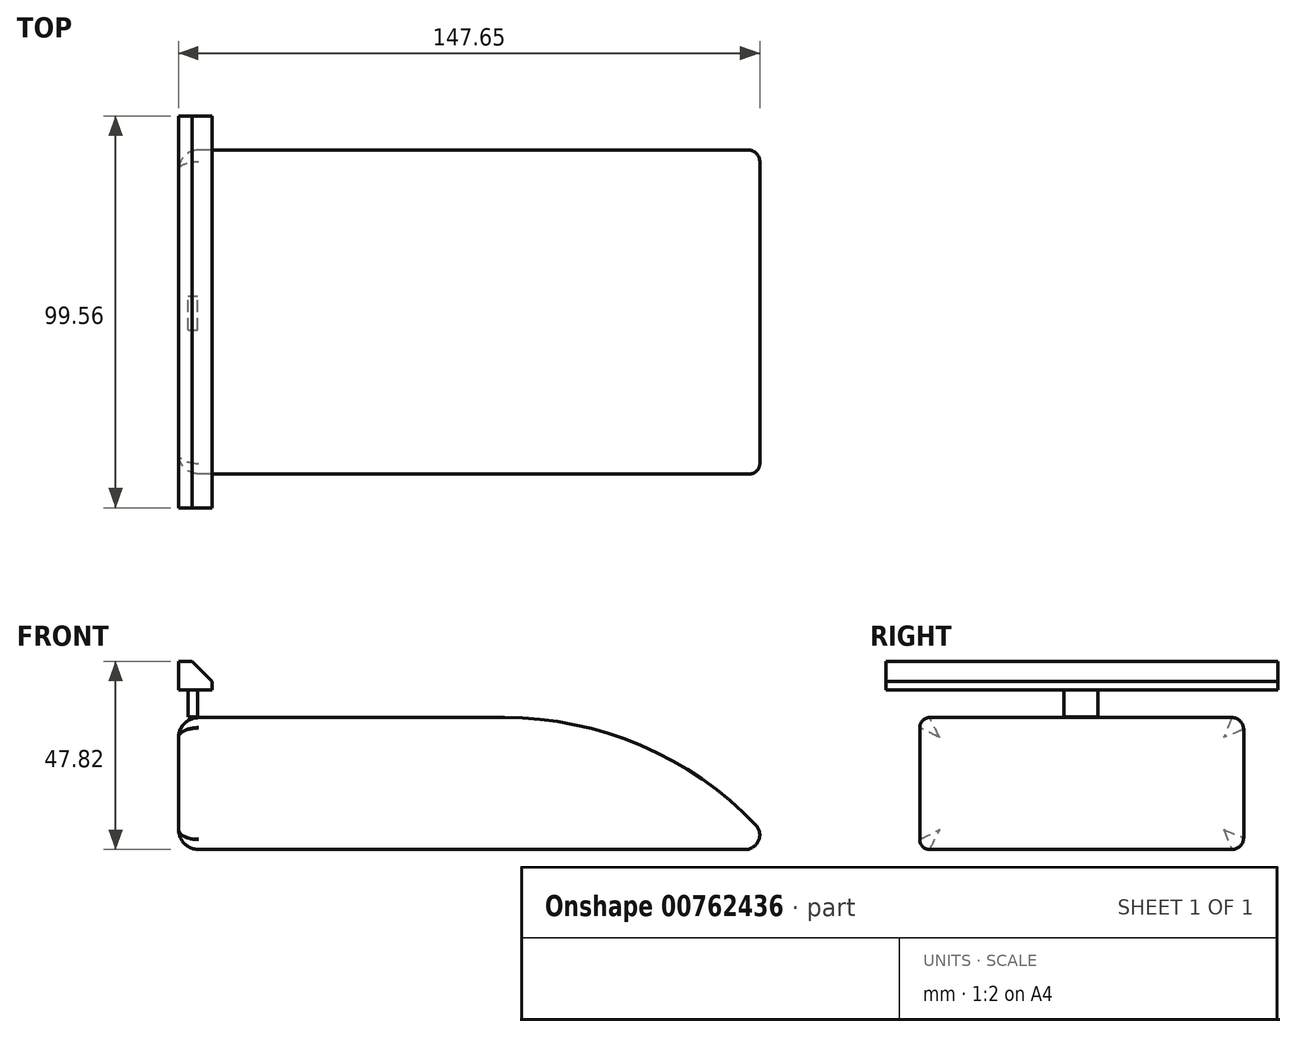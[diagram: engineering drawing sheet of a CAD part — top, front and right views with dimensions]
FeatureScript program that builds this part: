
annotation { "Feature Type Name" : "Feature", "Feature Type Description" : "" }
export const myFeature = defineFeature(function(context is Context, id is Id, definition is map)
    precondition{}
    {
        {
            var Q0;
            Q0=qCreatedBy(makeId("Front.planeOp"),FACE);
            var sketch = newSketch(context, id + "F0", { "sketchPlane" : qUnion([Q0])});
            skLineSegment(sketch, "E0.bottom", {"start": v(76.1, 0) * mm, "end": v(-76, 0) * mm});
            skLineSegment(sketch, "E0.top", {"start": v(76.1, 33.52) * mm, "end": v(-76, 33.52) * mm});
            skLineSegment(sketch, "E0.left", {"start": v(76.1, 0) * mm, "end": v(76.1, 33.52) * mm});
            skLineSegment(sketch, "E0.right", {"start": v(-76, 0) * mm, "end": v(-76, 33.52) * mm});
            skSolve(sketch);
        }
        {
            var Q0;
            Q0=makeQuery(id+"F0.imprint","IMPRINT",FACE,{"disambiguationData":[TD([[makeQuery(id+"F0.imprint","IMPRINT",EDGE,{"derivedFrom":sQuery(id+"F0.wireOp",EDGE,"E0.bottom")}),-1.0]])]});
            extrude(context, id + "F1", {"entities" : qUnion([Q0]), "depth" : 41.15 * mm, "offsetDistance" : 25.4 * mm});
        }
        {
            var Q0;
            Q0=makeQuery(id+"F1.opExtrude","CAP_FACE",FACE,{"disambiguationData":[OSD([sQuery(id+"F0.wireOp",EDGE,"E0.bottom"),sQuery(id+"F0.wireOp",EDGE,"E0.top"),sQuery(id+"F0.wireOp",EDGE,"E0.left"),sQuery(id+"F0.wireOp",EDGE,"E0.right")])],"isStart":true});
            extrude(context, id + "F2", {"entities" : qUnion([Q0]), "operationType" : NewBodyOperationType.ADD, "depth" : 41.15 * mm, "offsetDistance" : 25.4 * mm});
        }
        {
            var Q0;
            {var subQ0=sQuery(id+"F0.wireOp",EDGE,"E0.left");var subQ1=sQuery(id+"F0.wireOp",EDGE,"E0.top");Q0=makeQuery(id+"F2.boolean.opBoolean","MERGE",EDGE,{"derivedFrom":[makeQuery(id+"F1.opExtrude","SWEPT_EDGE",EDGE,{"disambiguationData":[OSD([subQ1,subQ0])]}),makeQuery(id+"F2.opExtrude","SWEPT_EDGE",EDGE,{"disambiguationData":[OSD([subQ1,subQ0])]})]});}
            fillet(context, id + "F3", {"entities" : qUnion([Q0]), "radius" : 88.3 * mm, "tangentPropagation" : true, "allowEdgeOverflow" : false});
        }
        {
            var Q0;
            Q0=qCreatedBy(makeId("Front.planeOp"),FACE);
            var sketch = newSketch(context, id + "F4", { "sketchPlane" : qUnion([Q0])});
            skLineSegment(sketch, "E1.bottom", {"start": v(-76, 47.82) * mm, "end": v(-67.5, 47.82) * mm});
            skLineSegment(sketch, "E1.top", {"start": v(-76, 40.52) * mm, "end": v(-67.5, 40.52) * mm});
            skLineSegment(sketch, "E1.left", {"start": v(-76, 47.82) * mm, "end": v(-76, 40.52) * mm});
            skLineSegment(sketch, "E1.right", {"start": v(-67.5, 47.82) * mm, "end": v(-67.5, 40.52) * mm});
            skSolve(sketch);
        }
        {
            var Q0;
            Q0=makeQuery(id+"F4.imprint","IMPRINT",FACE,{"disambiguationData":[TD([[makeQuery(id+"F4.imprint","IMPRINT",EDGE,{"derivedFrom":sQuery(id+"F4.wireOp",EDGE,"E1.bottom")}),-1.0]])]});
            extrude(context, id + "F5", {"entities" : qUnion([Q0]), "depth" : 49.78 * mm, "offsetDistance" : 25.4 * mm});
        }
        {
            var Q0;
            Q0=makeQuery(id+"F5.opExtrude","CAP_FACE",FACE,{"disambiguationData":[OSD([sQuery(id+"F4.wireOp",EDGE,"E1.bottom"),sQuery(id+"F4.wireOp",EDGE,"E1.top"),sQuery(id+"F4.wireOp",EDGE,"E1.left"),sQuery(id+"F4.wireOp",EDGE,"E1.right")])],"isStart":true});
            extrude(context, id + "F6", {"entities" : qUnion([Q0]), "operationType" : NewBodyOperationType.ADD, "depth" : 49.78 * mm, "offsetDistance" : 25.4 * mm});
        }
        {
            var Q0;
            Q0=qCreatedBy(makeId("Front.planeOp"),FACE);
            var sketch = newSketch(context, id + "F7", { "sketchPlane" : qUnion([Q0])});
            skLineSegment(sketch, "E2.bottom", {"start": v(-73.56, 40.56) * mm, "end": v(-71.16, 40.56) * mm});
            skLineSegment(sketch, "E2.top", {"start": v(-73.56, 33.66) * mm, "end": v(-71.16, 33.66) * mm});
            skLineSegment(sketch, "E2.left", {"start": v(-73.56, 40.56) * mm, "end": v(-73.56, 33.66) * mm});
            skLineSegment(sketch, "E2.right", {"start": v(-71.16, 40.56) * mm, "end": v(-71.16, 33.66) * mm});
            skSolve(sketch);
        }
        {
            var Q0;
            Q0 = qSketchRegion(id + "F7", true);
            extrude(context, id + "F8", {"entities" : qUnion([Q0]), "operationType" : NewBodyOperationType.ADD, "depth" : 4.57 * mm, "offsetDistance" : 25.4 * mm});
        }
        {
            var Q0;
            Q0 = qSketchRegion(id + "F7", true);
            extrude(context, id + "F9", {"entities" : qUnion([Q0]), "operationType" : NewBodyOperationType.ADD, "oppositeDirection" : true, "depth" : 4.06 * mm, "offsetDistance" : 25.4 * mm});
        }
        {
            var Q0;
            {var subQ0=sQuery(id+"F4.wireOp",EDGE,"E1.right");var subQ1=sQuery(id+"F4.wireOp",EDGE,"E1.bottom");Q0=makeQuery(id+"F6.boolean.opBoolean","MERGE",EDGE,{"derivedFrom":[makeQuery(id+"F5.opExtrude","SWEPT_EDGE",EDGE,{"disambiguationData":[OSD([subQ1,subQ0])]}),makeQuery(id+"F6.opExtrude","SWEPT_EDGE",EDGE,{"disambiguationData":[OSD([subQ1,subQ0])]})]});}
            chamfer(context, id + "F10", {"entities" : qUnion([Q0]), "width" : 5.08 * mm, "tangentPropagation" : true});
        }
        {
            var Q0;
            {var subQ0=sQuery(id+"F0.wireOp",EDGE,"E0.bottom");var subQ1=sQuery(id+"F0.wireOp",EDGE,"E0.left");var subQ2=sQuery(id+"F0.wireOp",EDGE,"E0.top");Q0=makeQuery(id+"F3.opFillet","BLEND_EDGE",EDGE,{"blendedFrom":[makeQuery(id+"F2.boolean.opBoolean","MERGE",EDGE,{"derivedFrom":[makeQuery(id+"F1.opExtrude","SWEPT_EDGE",EDGE,{"disambiguationData":[OSD([subQ2,subQ1])]}),makeQuery(id+"F2.opExtrude","SWEPT_EDGE",EDGE,{"disambiguationData":[OSD([subQ2,subQ1])]})]}),makeQuery(id+"F2.boolean.opBoolean","MERGE",FACE,{"derivedFrom":[makeQuery(id+"F1.opExtrude","SWEPT_FACE",FACE,{"disambiguationData":[OSD([subQ0])]}),makeQuery(id+"F2.opExtrude","SWEPT_FACE",FACE,{"disambiguationData":[OSD([subQ0])]})]})],"blendedInto":[makeQuery(id+"F2.boolean.opBoolean","MERGE",FACE,{"derivedFrom":[makeQuery(id+"F1.opExtrude","SWEPT_FACE",FACE,{"disambiguationData":[OSD([subQ0])]}),makeQuery(id+"F2.opExtrude","SWEPT_FACE",FACE,{"disambiguationData":[OSD([subQ0])]})]})]});}
            fillet(context, id + "F11", {"entities" : qUnion([Q0]), "radius" : 3.73 * mm, "tangentPropagation" : true, "allowEdgeOverflow" : false});
        }
        {
            var Q0;
            Q0=makeQuery(id+"F1.opExtrude","CAP_EDGE",EDGE,{"disambiguationData":[OSD([sQuery(id+"F0.wireOp",EDGE,"E0.top")])],"isStart":false});
            var Q1;
            {var subQ0=sQuery(id+"F0.wireOp",EDGE,"E0.left");var subQ1=sQuery(id+"F0.wireOp",EDGE,"E0.top");Q1=makeQuery(id+"F3.opFillet","BLEND_EDGE",EDGE,{"blendedFrom":[makeQuery(id+"F2.boolean.opBoolean","MERGE",EDGE,{"derivedFrom":[makeQuery(id+"F1.opExtrude","SWEPT_EDGE",EDGE,{"disambiguationData":[OSD([subQ1,subQ0])]}),makeQuery(id+"F2.opExtrude","SWEPT_EDGE",EDGE,{"disambiguationData":[OSD([subQ1,subQ0])]})]}),makeQuery(id+"F1.opExtrude","CAP_FACE",FACE,{"disambiguationData":[OSD([sQuery(id+"F0.wireOp",EDGE,"E0.bottom"),subQ1,subQ0,sQuery(id+"F0.wireOp",EDGE,"E0.right")])],"isStart":false})],"blendedInto":[makeQuery(id+"F1.opExtrude","CAP_FACE",FACE,{"disambiguationData":[OSD([sQuery(id+"F0.wireOp",EDGE,"E0.bottom"),subQ1,subQ0,sQuery(id+"F0.wireOp",EDGE,"E0.right")])],"isStart":false})]});}
            fillet(context, id + "F12", {"entities" : qUnion([Q0, Q1]), "radius" : 2.54 * mm, "tangentPropagation" : true, "allowEdgeOverflow" : false});
        }
        {
            var Q0;
            {var subQ0=sQuery(id+"F0.wireOp",EDGE,"E0.left");var subQ1=sQuery(id+"F0.wireOp",EDGE,"E0.top");Q0=makeQuery(id+"F3.opFillet","BLEND_EDGE",EDGE,{"blendedFrom":[makeQuery(id+"F2.boolean.opBoolean","MERGE",EDGE,{"derivedFrom":[makeQuery(id+"F1.opExtrude","SWEPT_EDGE",EDGE,{"disambiguationData":[OSD([subQ1,subQ0])]}),makeQuery(id+"F2.opExtrude","SWEPT_EDGE",EDGE,{"disambiguationData":[OSD([subQ1,subQ0])]})]}),makeQuery(id+"F2.opExtrude","CAP_FACE",FACE,{"disambiguationData":[OSD([sQuery(id+"F0.wireOp",EDGE,"E0.bottom"),subQ1,subQ0,sQuery(id+"F0.wireOp",EDGE,"E0.right")])],"isStart":false})],"blendedInto":[makeQuery(id+"F2.opExtrude","CAP_FACE",FACE,{"disambiguationData":[OSD([sQuery(id+"F0.wireOp",EDGE,"E0.bottom"),subQ1,subQ0,sQuery(id+"F0.wireOp",EDGE,"E0.right")])],"isStart":false})]});}
            var Q1;
            Q1=makeQuery(id+"F2.opExtrude","CAP_EDGE",EDGE,{"disambiguationData":[OSD([sQuery(id+"F0.wireOp",EDGE,"E0.top")])],"isStart":false});
            fillet(context, id + "F13", {"entities" : qUnion([Q0, Q1]), "radius" : 2.97 * mm, "tangentPropagation" : true, "allowEdgeOverflow" : false});
        }
        {
            var Q0;
            Q0=qCreatedBy(makeId("Front.planeOp"),FACE);
            var sketch = newSketch(context, id + "F14", { "sketchPlane" : qUnion([Q0])});
            skCircle(sketch, "E3", {"center": v(32.16, 11.58) * mm, "radius": 3.28 * mm});
            skCircle(sketch, "E4", {"center": v(-53.8, 11.58) * mm, "radius": 3.48 * mm});
            skSolve(sketch);
        }
        {
            var Q0;
            Q0=sQuery(id+"F14.wireOp",EDGE,"E4");
            extrude(context, id + "F15", {"bodyType" : ToolBodyType.SURFACE, "surfaceEntities" : qUnion([Q0]), "depth" : 49.02 * mm, "offsetDistance" : 25.4 * mm});
        }
        {
            var Q0;
            Q0=sQuery(id+"F14.wireOp",EDGE,"E3");
            extrude(context, id + "F16", {"bodyType" : ToolBodyType.SURFACE, "surfaceEntities" : qUnion([Q0]), "depth" : 49.02 * mm, "offsetDistance" : 25.4 * mm});
        }
        {
            var Q0;
            Q0=sQuery(id+"F14.wireOp",EDGE,"E3");
            var Q1;
            Q1=sQuery(id+"F14.wireOp",EDGE,"E4");
            extrude(context, id + "F17", {"bodyType" : ToolBodyType.SURFACE, "surfaceOperationType" : NewSurfaceOperationType.ADD, "surfaceEntities" : qUnion([Q0, Q1]), "oppositeDirection" : true, "depth" : 49.02 * mm, "offsetDistance" : 25.4 * mm});
        }
        {
            var Q0;
            {var subQ0=sQuery(id+"F0.wireOp",EDGE,"E0.right");Q0=makeQuery(id+"F2.boolean.opBoolean","MERGE",FACE,{"derivedFrom":[makeQuery(id+"F1.opExtrude","SWEPT_FACE",FACE,{"disambiguationData":[OSD([subQ0])]}),makeQuery(id+"F2.opExtrude","SWEPT_FACE",FACE,{"disambiguationData":[OSD([subQ0])]})]});}
            fillet(context, id + "F18", {"entities" : qUnion([Q0]), "radius" : 5.08 * mm, "tangentPropagation" : true, "allowEdgeOverflow" : false});
        }
    });
